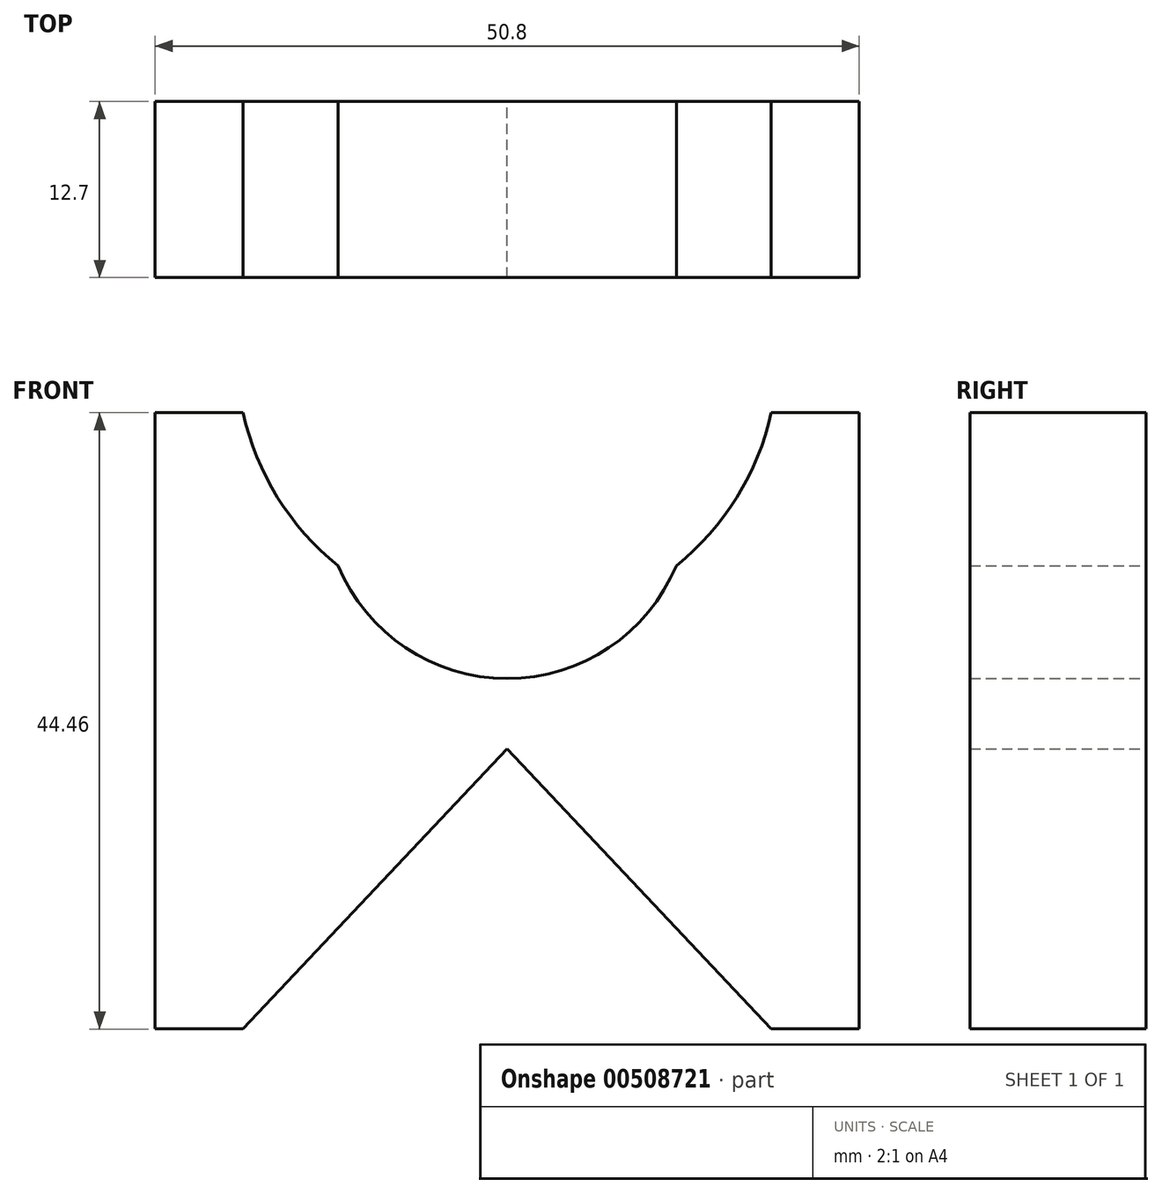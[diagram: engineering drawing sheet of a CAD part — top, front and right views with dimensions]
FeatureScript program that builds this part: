
annotation { "Feature Type Name" : "Feature", "Feature Type Description" : "" }
export const myFeature = defineFeature(function(context is Context, id is Id, definition is map)
    precondition{}
    {
        {
            var Q0;
            Q0=qCreatedBy(makeId("Front.planeOp"),FACE);
            var sketch = newSketch(context, id + "F0", { "sketchPlane" : qUnion([Q0])});
            skPoint(sketch, "E0.middle", {"position": v(0, 0) * mm});
            skLineSegment(sketch, "E1.bottom", {"start": v(25.4, -22.23) * mm, "end": v(-25.4, -22.23) * mm});
            skLineSegment(sketch, "E1.top", {"start": v(25.4, 22.23) * mm, "end": v(-25.4, 22.23) * mm});
            skLineSegment(sketch, "E1.left", {"start": v(25.4, -22.23) * mm, "end": v(25.4, 22.23) * mm});
            skLineSegment(sketch, "E1.right", {"start": v(-25.4, -22.23) * mm, "end": v(-25.4, 22.22) * mm});
            skPoint(sketch, "E2", {"position": v(0, 26.42) * mm});
            skArc(sketch, "E3", {"start": v(-19.05, 22.22) * mm, "mid": v(0, 6.91) * mm, "end": v(19.05, 22.23) * mm});
            skPoint(sketch, "E4", {"position": v(0, 16.26) * mm});
            skArc(sketch, "E5", {"start": v(12.2, 11.2) * mm, "mid": v(0, 3.05) * mm, "end": v(-12.2, 11.2) * mm});
            skLineSegment(sketch, "E6", {"start": v(-19.05, -22.23) * mm, "end": v(0, -2.02) * mm});
            skPoint(sketch, "E6.endSnap0", {"position": v(0, 3.05) * mm});
            skLineSegment(sketch, "E7", {"start": v(0, -2.02) * mm, "end": v(19.05, -22.23) * mm});
            skSolve(sketch);
        }
        {
            var Q0;
            {var subQ7=sQuery(id+"F0.wireOp",EDGE,"E1.left");Q0=makeQuery(id+"F0.imprint","IMPRINT",FACE,{"disambiguationData":[TD([[makeQuery(id+"F0.imprint","IMPRINT",EDGE,{"derivedFrom":subQ7}),1.0]])]});}
            extrude(context, id + "F1", {"entities" : qUnion([Q0]), "depth" : 12.7 * mm});
        }
    });
